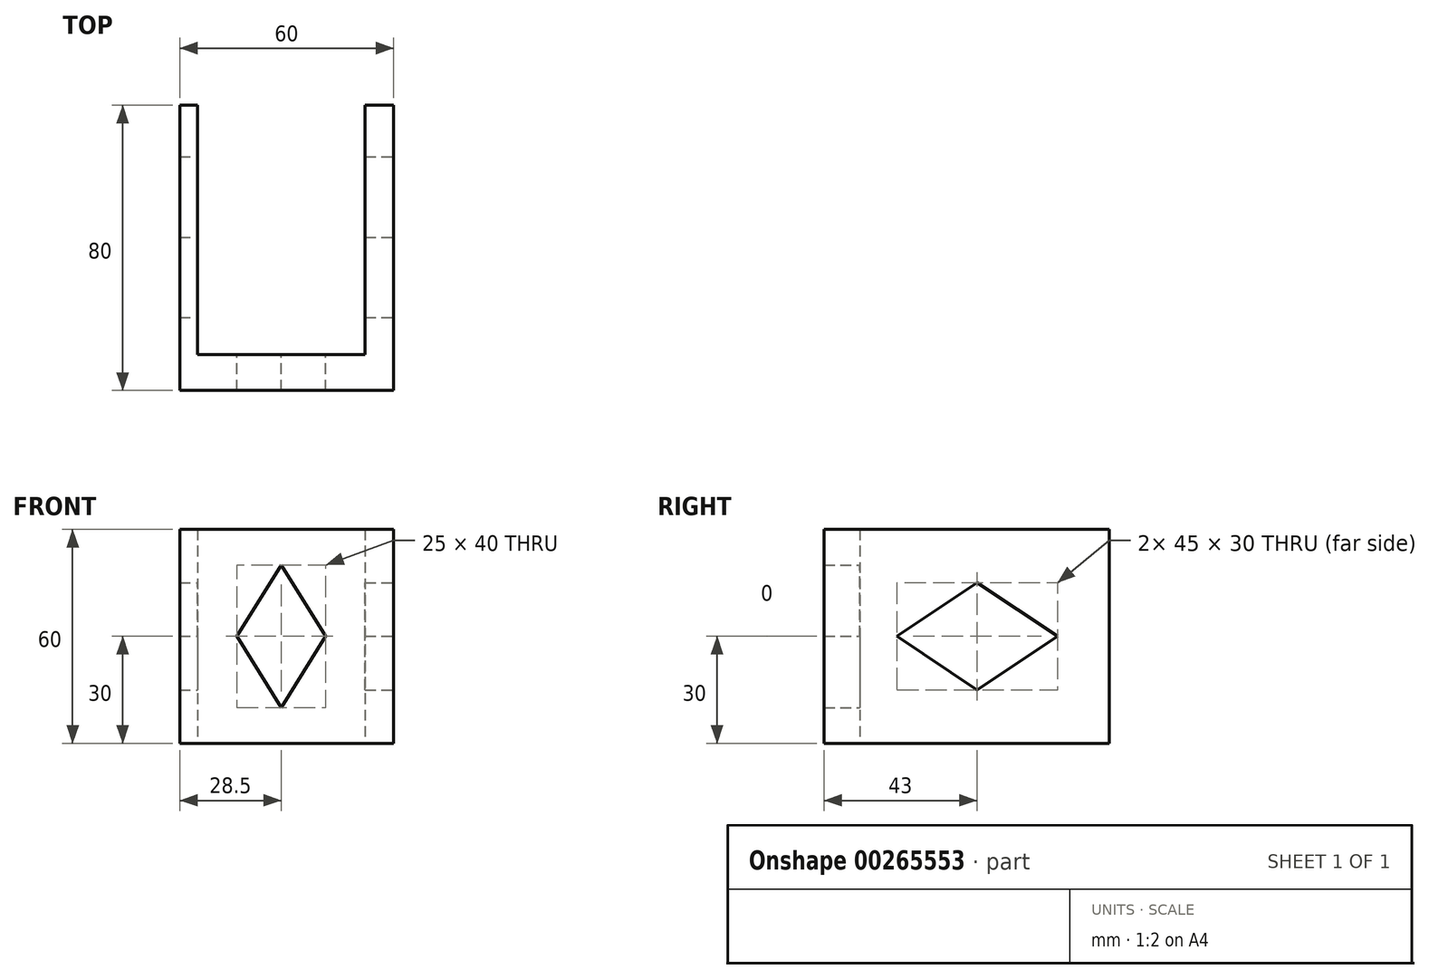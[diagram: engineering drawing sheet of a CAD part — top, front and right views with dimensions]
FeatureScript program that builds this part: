
annotation { "Feature Type Name" : "Feature", "Feature Type Description" : "" }
export const myFeature = defineFeature(function(context is Context, id is Id, definition is map)
    precondition{}
    {
        {
            var Q0;
            Q0=qCreatedBy(makeId("Top.planeOp"),FACE);
            var sketch = newSketch(context, id + "F0", { "sketchPlane" : qUnion([Q0])});
            skLineSegment(sketch, "E0.bottom", {"start": v(-30, -40) * mm, "end": v(30, -40) * mm});
            skLineSegment(sketch, "E0.top", {"start": v(-30, 40) * mm, "end": v(-25, 40) * mm});
            skLineSegment(sketch, "E0.left", {"start": v(-30, -40) * mm, "end": v(-30, 40) * mm});
            skLineSegment(sketch, "E0.right", {"start": v(30, -40) * mm, "end": v(30, 40) * mm});
            skLineSegment(sketch, "E1.top", {"start": v(-25, -30) * mm, "end": v(22, -30) * mm});
            skLineSegment(sketch, "E1.left", {"start": v(-25, 36) * mm, "end": v(-25, -30) * mm});
            skLineSegment(sketch, "E1.right", {"start": v(22, 36) * mm, "end": v(22, -30) * mm});
            skLineSegment(sketch, "E2", {"start": v(-30, 40) * mm, "end": v(30, -40) * mm, "construction": true});
            skLineSegment(sketch, "E3", {"start": v(-25, 36) * mm, "end": v(-25, 40) * mm});
            skLineSegment(sketch, "E4", {"start": v(22, 36) * mm, "end": v(22, 40) * mm});
            skLineSegment(sketch, "E5.trimOffspring", {"start": v(22, 40) * mm, "end": v(30, 40) * mm});
            skSolve(sketch);
        }
        {
            var Q0;
            Q0=qSketchRegion(id+"F0",true);
            extrude(context, id + "F1", {"entities" : qUnion([Q0]), "depth" : 60 * mm});
        }
        {
            var Q0;
            Q0=makeQuery(id+"F1.opExtrude","SWEPT_FACE",FACE,{"disambiguationData":[OSD([sQuery(id+"F0.wireOp",EDGE,"E0.right")])]});
            var sketch = newSketch(context, id + "F2", { "sketchPlane" : qUnion([Q0])});
            skLineSegment(sketch, "E6", {"start": v(-19.5, 30) * mm, "end": v(3, 45) * mm});
            skLineSegment(sketch, "E7", {"start": v(3, 45) * mm, "end": v(25.5, 30) * mm});
            skLineSegment(sketch, "E8", {"start": v(25.5, 30) * mm, "end": v(3, 15) * mm});
            skLineSegment(sketch, "E9", {"start": v(3, 15) * mm, "end": v(-19.5, 30) * mm});
            skLineSegment(sketch, "E10", {"start": v(3, 45) * mm, "end": v(3, 15) * mm, "construction": true});
            skLineSegment(sketch, "E11", {"start": v(-19.5, 30) * mm, "end": v(25.5, 30) * mm, "construction": true});
            skLineSegment(sketch, "E12.0.1", {"start": v(-30, 0) * mm, "end": v(-30, 60) * mm});
            skLineSegment(sketch, "E12.0.3", {"start": v(-30, 60) * mm, "end": v(-30, 0) * mm});
            skLineSegment(sketch, "E13.0.1", {"start": v(36, 0) * mm, "end": v(36, 60) * mm});
            skLineSegment(sketch, "E13.0.3", {"start": v(36, 60) * mm, "end": v(36, 0) * mm});
            skLineSegment(sketch, "E14", {"start": v(-19.5, 30) * mm, "end": v(-30, 30) * mm});
            skLineSegment(sketch, "E15", {"start": v(25.5, 30) * mm, "end": v(36, 30) * mm});
            skLineSegment(sketch, "E16", {"start": v(3, 45) * mm, "end": v(3, 60) * mm});
            skLineSegment(sketch, "E17", {"start": v(3, 15) * mm, "end": v(3, 0) * mm});
            skSolve(sketch);
        }
        {
            var Q0;
            Q0=qSketchRegion(id+"F2",true);
            extrude(context, id + "F3", {"entities" : qUnion([Q0]), "operationType" : NewBodyOperationType.REMOVE, "endBound" : BoundingType.THROUGH_ALL, "oppositeDirection" : true, "depth" : 25 * mm});
        }
        {
            var Q0;
            Q0=makeQuery(id+"F1.opExtrude","SWEPT_FACE",FACE,{"disambiguationData":[OSD([sQuery(id+"F0.wireOp",EDGE,"E0.top")])]});
            var sketch = newSketch(context, id + "F4", { "sketchPlane" : qUnion([Q0])});
            skLineSegment(sketch, "E18.0.1", {"start": v(-22, 0) * mm, "end": v(-22, 60) * mm});
            skLineSegment(sketch, "E18.0.3", {"start": v(-22, 0) * mm, "end": v(-22, 60) * mm});
            skLineSegment(sketch, "E19.0.1", {"start": v(25, 60) * mm, "end": v(25, 0) * mm});
            skLineSegment(sketch, "E19.0.3", {"start": v(25, 60) * mm, "end": v(25, 0) * mm});
            skLineSegment(sketch, "E20.2.0.0", {"start": v(1.5, 50) * mm, "end": v(14, 30) * mm});
            skLineSegment(sketch, "E20.2.0.1", {"start": v(-11, 30) * mm, "end": v(1.5, 50) * mm});
            skLineSegment(sketch, "E20.2.0.2", {"start": v(14, 30) * mm, "end": v(1.5, 10) * mm});
            skLineSegment(sketch, "E20.2.0.3", {"start": v(1.5, 50) * mm, "end": v(1.5, 10) * mm, "construction": true});
            skLineSegment(sketch, "E20.2.0.4", {"start": v(1.5, 10) * mm, "end": v(-11, 30) * mm});
            skLineSegment(sketch, "E20.2.0.5", {"start": v(-11, 30) * mm, "end": v(14, 30) * mm, "construction": true});
            skLineSegment(sketch, "E21", {"start": v(14, 30) * mm, "end": v(25, 30) * mm, "construction": true});
            skLineSegment(sketch, "E22", {"start": v(-11, 30) * mm, "end": v(-22, 30) * mm, "construction": true});
            skLineSegment(sketch, "E23", {"start": v(1.5, 50) * mm, "end": v(1.5, 60) * mm, "construction": true});
            skLineSegment(sketch, "E24", {"start": v(1.5, 10) * mm, "end": v(1.5, 0) * mm, "construction": true});
            skSolve(sketch);
        }
        {
            var Q0;
            Q0=qSketchRegion(id+"F4",true);
            extrude(context, id + "F5", {"entities" : qUnion([Q0]), "operationType" : NewBodyOperationType.REMOVE, "endBound" : BoundingType.THROUGH_ALL, "oppositeDirection" : true, "depth" : 25 * mm});
        }
    });
